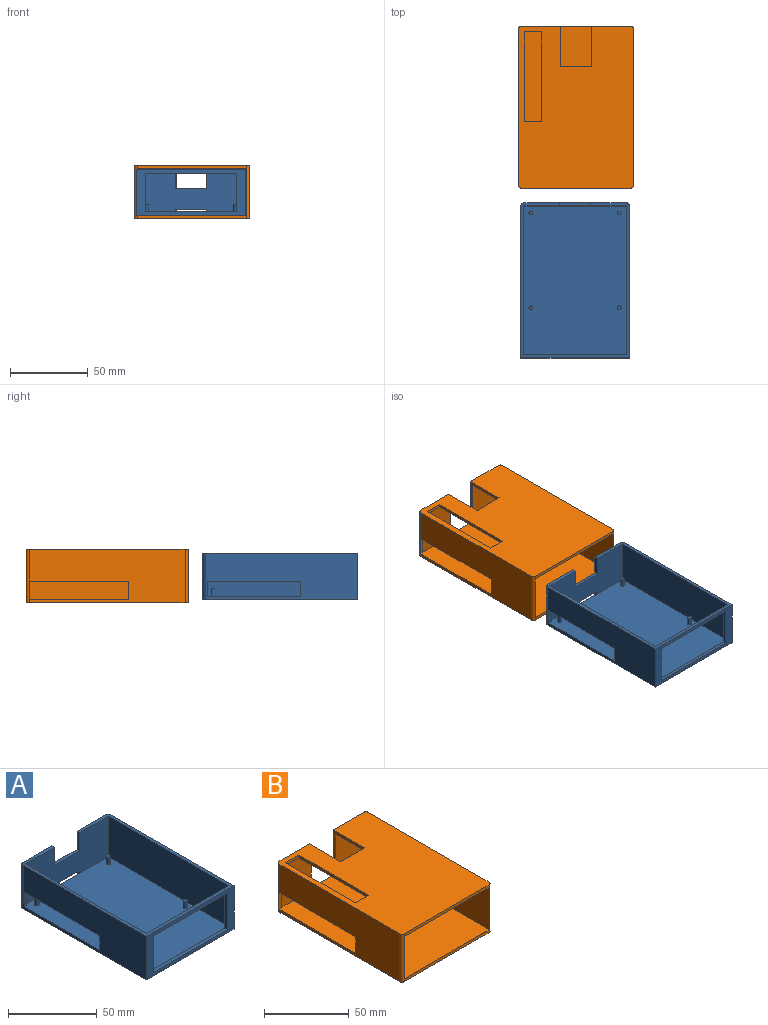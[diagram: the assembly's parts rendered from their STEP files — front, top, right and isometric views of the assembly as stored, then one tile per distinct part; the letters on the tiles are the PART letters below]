
ASSEMBLY  parts=2 mates=1
PART A: 35 faces, bbox 70x100x30 mm
  f0: plane 98x30mm, normal (-1,0,0), area 2340mm2, adj f1,f3,f9,f10,f30,f31,f32,f34
  f1: plane 100x70mm, normal (0,0,1), area 622.3mm2, adj f0,f2,f4,f5,f6,f7,f8,f9
  f2: plane 66x30mm, normal (0,1,0), area 1650mm2, adj f1,f3,f23,f24,f25,f27,f28,f29
  f3: plane 100x70mm, normal (0,0,-1), area 6958.3mm2, adj f0,f2,f8,f9,f23,f25,f26,f33
  f4: plane 66x28mm, normal (0,-1,0), area 1558mm2, adj f1,f5,f7,f10,f23,f24,f25,f27
  f5: plane 96x28mm, normal (1,0,0), area 2088mm2, adj f1,f4,f6,f10,f30,f31,f32
  f6: plane 66x28mm, normal (0,1,0), area 373mm2, adj f1,f5,f7,f10,f19,f20,f21,f22
  f7: plane 96x28mm, normal (-1,0,0), area 2688mm2, adj f1,f4,f6,f10
  f8: plane 98x30mm, normal (1,0,0), area 2940mm2, adj f1,f3,f9,f33
  f9: plane 70x30mm, normal (0,-1,0), area 625mm2, adj f0,f1,f3,f8,f19,f20,f21,f22
  f10: plane 96x68mm, normal (0,0,1), area 6436.4mm2, adj f0,f4,f5,f6,f7,f11,f13,f15
  f11: cylinder r=1.25mm len=5mm, axis (0,0,-1), area 39.3mm2, adj f10,f12
  f12: plane 2.5x2.5mm, normal (0,0,1), area 4.9mm2, adj f11
  f13: cylinder r=1.25mm len=5mm, axis (0,0,-1), area 39.3mm2, adj f10,f14
  f14: plane 2.5x2.5mm, normal (0,0,1), area 4.9mm2, adj f13
  f15: cylinder r=1.25mm len=5mm, axis (0,0,-1), area 39.3mm2, adj f10,f16
  f16: plane 2.5x2.5mm, normal (0,0,1), area 4.9mm2, adj f15
  f17: cylinder r=1.25mm len=5mm, axis (0,0,-1), area 39.3mm2, adj f10,f18
  f18: plane 2.5x2.5mm, normal (0,0,1), area 4.9mm2, adj f17
  f19: plane 59x2mm, normal (0,0,-1), area 118mm2, adj f6,f9,f20,f22
  f20: plane 25x2mm, normal (1,0,0), area 50mm2, adj f6,f9,f19,f21
  f21: plane 59x2mm, normal (0,0,1), area 118mm2, adj f6,f9,f20,f22
  f22: plane 25x2mm, normal (-1,0,0), area 50mm2, adj f6,f9,f19,f21
  f23: plane 4x2mm, normal (1,0,0), area 8mm2, adj f2,f3,f4,f24,f26
  f24: plane 20x2mm, normal (0,0,-1), area 40mm2, adj f2,f4,f23,f25
  f25: plane 4x2mm, normal (-1,0,0), area 8mm2, adj f2,f3,f4,f24,f26
  f26: plane 20x2mm, normal (0,1,0), area 40mm2, adj f3,f10,f23,f25
  f27: plane 20x2mm, normal (0,0,1), area 40mm2, adj f2,f4,f28,f29
  f28: plane 12.5x2mm, normal (1,0,0), area 25mm2, adj f1,f2,f4,f27
  f29: plane 12.5x2mm, normal (-1,0,0), area 25mm2, adj f1,f2,f4,f27
  f30: plane 60x2mm, normal (0,0,-1), area 120mm2, adj f0,f5,f31,f32
  f31: plane 10x2mm, normal (0,-1,0), area 20mm2, adj f0,f5,f10,f30
  f32: plane 10x2mm, normal (0,1,0), area 20mm2, adj f0,f5,f10,f30
  f33: cylinder r=2mm len=30mm, axis (0,0,1), area 94.2mm2, adj f1,f2,f3,f8
  f34: cylinder r=2mm len=30mm, axis (0,0,-1), area 94.2mm2, adj f0,f1,f2,f3
PART B: 27 faces, bbox 74.5x104.5x34.5 mm
  f0: plane 102.69x30.5mm, normal (1,0,0), area 2364mm2, adj f5,f14,f15,f16,f17,f25,f26
  f1: plane 70.5x2mm, normal (0,-1,0), area 141mm2, adj f5,f6,f22,f25
  f2: plane 11x2mm, normal (0,-1,0), area 22mm2, adj f3,f15,f20,f21
  f3: plane 104.5x74.5mm, normal (0,0,1), area 6623.8mm2, adj f2,f4,f7,f8,f9,f10,f11,f18
  f4: plane 100.5x34.5mm, normal (-1,0,0), area 2699.2mm2, adj f3,f5,f6,f16,f24,f25,f26
  f5: plane 104.5x72.7mm, normal (0,0,1), area 7432.6mm2, adj f0,f1,f4,f9,f10,f11,f12,f13
  f6: plane 104.5x74.5mm, normal (0,0,-1), area 7781.8mm2, adj f1,f4,f8,f9,f22,f23,f24,f25
  f7: plane 70.5x2mm, normal (0,-1,0), area 141mm2, adj f3,f15,f22,f25
  f8: plane 100.5x34.5mm, normal (1,0,0), area 3467.3mm2, adj f3,f6,f22,f23
  f9: plane 70.5x34.5mm, normal (0,1,0), area 1782.2mm2, adj f3,f5,f6,f10,f11,f23,f24
  f10: plane 32.5x26mm, normal (-1,0,0), area 106.9mm2, adj f3,f5,f9,f12,f15,f18
  f11: plane 32.5x26mm, normal (1,0,0), area 106.9mm2, adj f3,f5,f9,f14,f15,f18
  f12: plane 30.5x25.45mm, normal (0,-1,0), area 776.2mm2, adj f5,f10,f13,f15
  f13: plane 102.69x30.5mm, normal (-1,0,0), area 3132mm2, adj f5,f12,f15,f22
  f14: plane 30.5x25.45mm, normal (0,-1,0), area 776.2mm2, adj f0,f5,f11,f15
  f15: plane 102.7x70.9mm, normal (0,0,-1), area 6159.4mm2, adj f0,f2,f7,f10,f11,f12,f13,f14
  f16: plane 64x1.8mm, normal (0,0,-1), area 115.2mm2, adj f0,f4,f17,f26
  f17: plane 12x1.8mm, normal (0,-1,0), area 21.6mm2, adj f0,f5,f16,f24
  f18: plane 20x2mm, normal (0,1,0), area 40mm2, adj f3,f10,f11,f15
  f19: plane 11x2mm, normal (0,1,0), area 22mm2, adj f3,f15,f20,f21
  f20: plane 58x2mm, normal (-1,0,0), area 116mm2, adj f2,f3,f15,f19
  f21: plane 58x2mm, normal (1,0,0), area 116mm2, adj f2,f3,f15,f19
  f22: cylinder r=2mm len=34.5mm, axis (0,0,-1), area 102.3mm2, adj f1,f3,f5,f6,f7,f8,f13,f15
  f23: cylinder r=2mm len=34.5mm, axis (0,0,1), area 108.4mm2, adj f3,f6,f8,f9
  f24: cylinder r=2mm len=34.5mm, axis (0,0,-1), area 108.4mm2, adj f3,f4,f6,f9,f17
  f25: cylinder r=2mm len=34.5mm, axis (0,0,1), area 102.3mm2, adj f0,f1,f3,f4,f5,f6,f7,f15
  f26: plane 12x1.8mm, normal (0,1,0), area 21.6mm2, adj f0,f4,f5,f16
PLACE A rot(axis=(1,0,0),0deg) t=(-9.22,-93.14,82.72)mm
PLACE B rot(axis=(1,0,0),0deg) t=(-8.66,18.62,80.72)mm
MATE planar B.f5 <-> A.f3  axis (0,0,1) through (-9.22,18.27,82.72)mm
